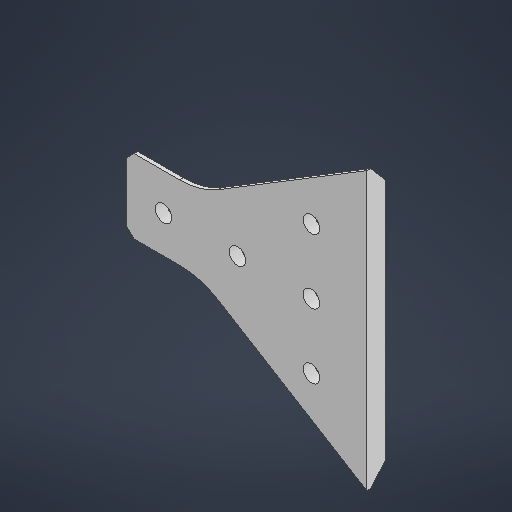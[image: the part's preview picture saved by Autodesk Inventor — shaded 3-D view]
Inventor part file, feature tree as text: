
AUTODESK INVENTOR PART (.ipt)
format: ipt  version: 2025.1 (Build 291241000, 241)  size: 410,112 bytes
history: native  units: mm
features: chamfer x2, sketch x1, extrude x1, hole x1, fillet x1
ambient origin geometry x8: Origin, YZ Plane, XZ Plane, XY Plane, X Axis, Y Axis, Z Axis, Center Point
bodies: Solid1 (feature_tree)
feature tree (6):
  sketch  "Sketch1"  dims[d0=20.0mm d1=65.0mm d2=50.0mm d4=20.0mm d5=75.0mm d6=35.0mm d7=5.0mm d8=0.0mm d9=40.0mm d10=4.5mm d11=6.0mm d12=8.0mm d13=2.0mm d14=90.0deg d15=8.0mm d16=20.594885mm d17=20.0mm d18=2.0mm d19=2.0mm d20=45.0deg d21=25.0mm d22=5.0mm d23=4.5mm d27=4.0mm d28=2.0mm d29=45.0deg d30=20.0mm]
  extrude  "Extrusion1"  Depth=65.0mm
  hole  "Hole1"  [1 undecoded]
  fillet  "Fillet1"  Radius=20.0mm
  chamfer  "Chamfer1"  Distance=75.0mm
  chamfer  "Chamfer3"  Distance=35.0mm
note: 1 required parameter value undecoded (feature->parameter linkage not recoverable at this tier; creation-order binding heuristic only, values carry confidence <= 0.55)
